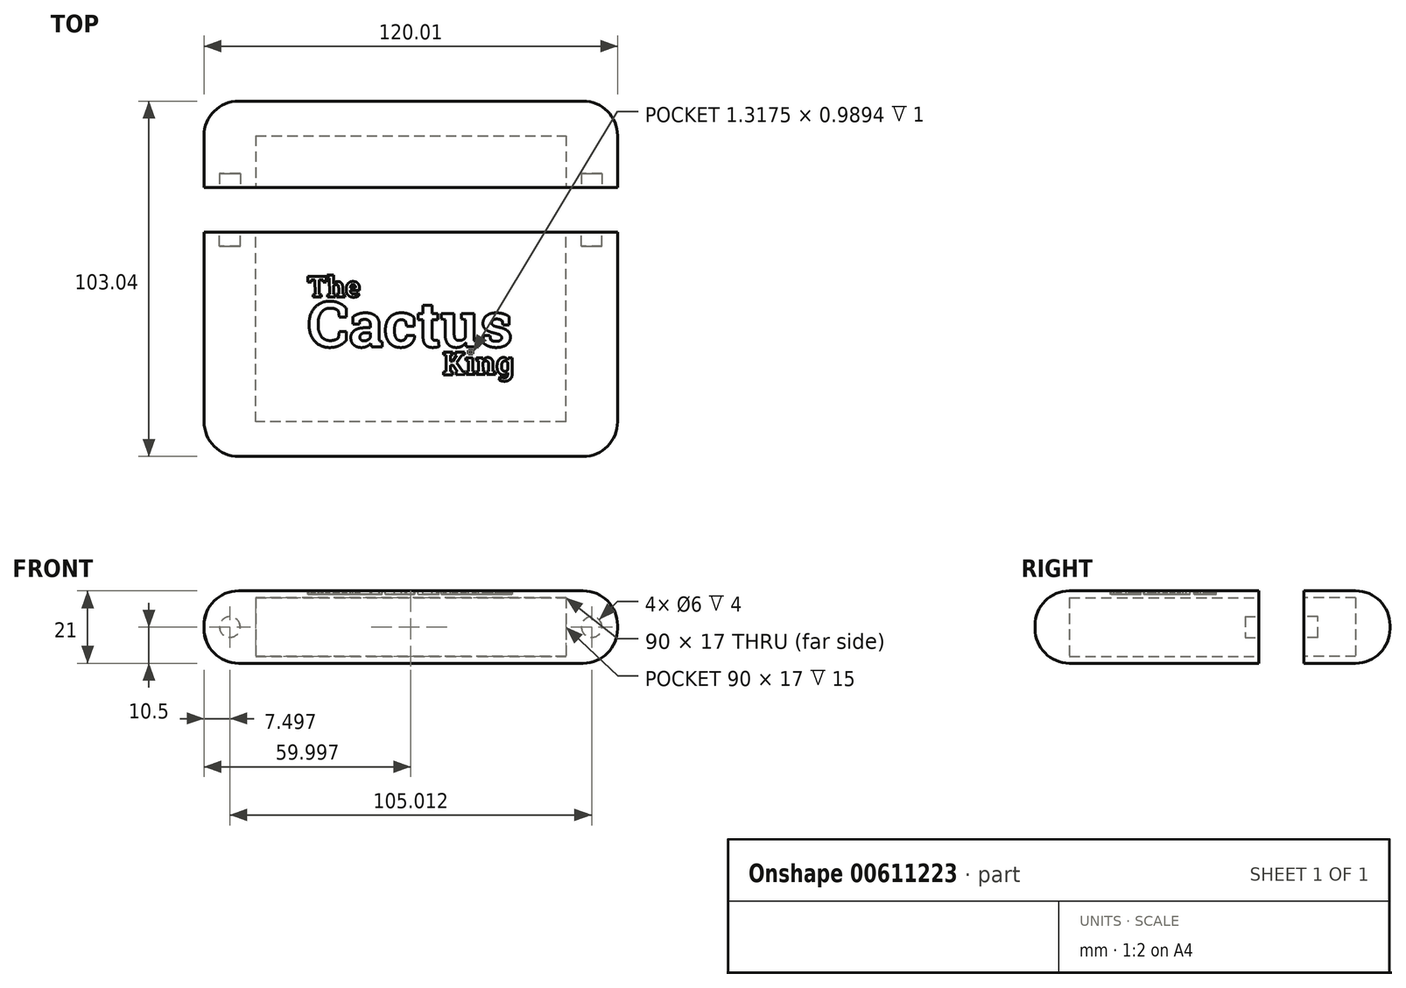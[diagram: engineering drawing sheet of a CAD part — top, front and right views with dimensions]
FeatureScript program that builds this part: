
annotation { "Feature Type Name" : "Feature", "Feature Type Description" : "" }
export const myFeature = defineFeature(function(context is Context, id is Id, definition is map)
    precondition{}
    {
        {
            var Q0;
            Q0=qCreatedBy(makeId("Top.planeOp"),FACE);
            var sketch = newSketch(context, id + "F0", { "sketchPlane" : qUnion([Q0])});
            skLineSegment(sketch, "E0.top", {"start": v(-57.38, -31.8) * mm, "end": v(62.62, -31.8) * mm});
            skLineSegment(sketch, "E0.left", {"start": v(-57.38, 33.2) * mm, "end": v(-57.38, -31.8) * mm});
            skLineSegment(sketch, "E0.right", {"start": v(62.62, 33.2) * mm, "end": v(62.62, -31.8) * mm});
            skLineSegment(sketch, "E1", {"start": v(-57.38, 33.2) * mm, "end": v(62.62, 33.2) * mm});
            skSolve(sketch);
        }
        {
            var Q0;
            Q0=qCreatedBy(makeId("Top.planeOp"),FACE);
            var sketch = newSketch(context, id + "F1", { "sketchPlane" : qUnion([Q0])});
            skLineSegment(sketch, "E2.bottom", {"start": v(-57.4, 71.24) * mm, "end": v(62.6, 71.24) * mm});
            skLineSegment(sketch, "E2.top", {"start": v(-57.4, 46.24) * mm, "end": v(62.6, 46.24) * mm});
            skLineSegment(sketch, "E2.left", {"start": v(-57.4, 71.24) * mm, "end": v(-57.4, 46.24) * mm});
            skLineSegment(sketch, "E2.right", {"start": v(62.6, 71.24) * mm, "end": v(62.6, 46.24) * mm});
            skSolve(sketch);
        }
        {
            var Q0;
            Q0=makeQuery(id+"F1.imprint","IMPRINT",FACE,{"disambiguationData":[TD([[makeQuery(id+"F1.imprint","IMPRINT",EDGE,{"derivedFrom":sQuery(id+"F1.wireOp",EDGE,"E2.bottom")}),-1.0]])]});
            extrude(context, id + "F2", {"entities" : qUnion([Q0]), "depth" : 21 * mm, "offsetDistance" : 25 * mm});
        }
        {
            var Q0;
            Q0=makeQuery(id+"F2.opExtrude","SWEPT_EDGE",EDGE,{"disambiguationData":[OSD([sQuery(id+"F1.wireOp",EDGE,"E2.bottom"),sQuery(id+"F1.wireOp",EDGE,"E2.right")])]});
            var Q1;
            Q1=makeQuery(id+"F2.opExtrude","SWEPT_EDGE",EDGE,{"disambiguationData":[OSD([sQuery(id+"F1.wireOp",EDGE,"E2.bottom"),sQuery(id+"F1.wireOp",EDGE,"E2.left")])]});
            var Q2;
            Q2=makeQuery(id+"F2.opExtrude","CAP_EDGE",EDGE,{"disambiguationData":[OSD([sQuery(id+"F1.wireOp",EDGE,"E2.bottom")])],"isStart":false});
            var Q3;
            Q3=makeQuery(id+"F2.opExtrude","CAP_EDGE",EDGE,{"disambiguationData":[OSD([sQuery(id+"F1.wireOp",EDGE,"E2.bottom")])],"isStart":true});
            var Q4;
            Q4=makeQuery(id+"F2.opExtrude","CAP_EDGE",EDGE,{"disambiguationData":[OSD([sQuery(id+"F1.wireOp",EDGE,"E2.left")])],"isStart":true});
            var Q5;
            Q5=makeQuery(id+"F2.opExtrude","CAP_EDGE",EDGE,{"disambiguationData":[OSD([sQuery(id+"F1.wireOp",EDGE,"E2.left")])],"isStart":false});
            var Q6;
            Q6=makeQuery(id+"F2.opExtrude","CAP_EDGE",EDGE,{"disambiguationData":[OSD([sQuery(id+"F1.wireOp",EDGE,"E2.right")])],"isStart":false});
            var Q7;
            Q7=makeQuery(id+"F2.opExtrude","CAP_EDGE",EDGE,{"disambiguationData":[OSD([sQuery(id+"F1.wireOp",EDGE,"E2.right")])],"isStart":true});
            fillet(context, id + "F3", {"entities" : qUnion([Q0, Q1, Q2, Q3, Q4, Q5, Q6, Q7]), "radius" : 10 * mm, "tangentPropagation" : true, "allowEdgeOverflow" : false});
        }
        {
            var Q0;
            Q0=makeQuery(id+"F2.opExtrude","SWEPT_FACE",FACE,{"disambiguationData":[OSD([sQuery(id+"F1.wireOp",EDGE,"E2.top")])]});
            var sketch = newSketch(context, id + "F4", { "sketchPlane" : qUnion([Q0])});
            skLineSegment(sketch, "E3.bottom", {"start": v(-42.4, 19) * mm, "end": v(47.6, 19) * mm});
            skLineSegment(sketch, "E3.top", {"start": v(-42.4, 2) * mm, "end": v(47.6, 2) * mm});
            skLineSegment(sketch, "E3.left", {"start": v(-42.4, 19) * mm, "end": v(-42.4, 2) * mm});
            skLineSegment(sketch, "E3.right", {"start": v(47.6, 19) * mm, "end": v(47.6, 2) * mm});
            skSolve(sketch);
        }
        {
            var Q0;
            Q0=makeQuery(id+"F4.imprint","IMPRINT",FACE,{"disambiguationData":[TD([[makeQuery(id+"F4.imprint","IMPRINT",EDGE,{"derivedFrom":sQuery(id+"F4.wireOp",EDGE,"E3.bottom")}),-1.0]])]});
            extrude(context, id + "F5", {"entities" : qUnion([Q0]), "operationType" : NewBodyOperationType.REMOVE, "oppositeDirection" : true, "depth" : 15 * mm, "offsetDistance" : 25 * mm});
        }
        {
            var Q0;
            Q0=makeQuery(id+"F2.opExtrude","SWEPT_FACE",FACE,{"disambiguationData":[OSD([sQuery(id+"F1.wireOp",EDGE,"E2.top")])]});
            var sketch = newSketch(context, id + "F6", { "sketchPlane" : qUnion([Q0])});
            skCircle(sketch, "E4", {"center": v(-49.9, 10.5) * mm, "radius": 3 * mm});
            skCircle(sketch, "E5", {"center": v(55.1, 10.5) * mm, "radius": 3 * mm});
            skSolve(sketch);
        }
        {
            var Q0;
            Q0=makeQuery(id+"F6.imprint","IMPRINT",FACE,{"disambiguationData":[TD([[makeQuery(id+"F6.imprint","IMPRINT",EDGE,{"derivedFrom":sQuery(id+"F6.wireOp",EDGE,"E5")}),1.0]])]});
            var Q1;
            Q1=makeQuery(id+"F6.imprint","IMPRINT",FACE,{"disambiguationData":[TD([[makeQuery(id+"F6.imprint","IMPRINT",EDGE,{"derivedFrom":sQuery(id+"F6.wireOp",EDGE,"E4")}),1.0]])]});
            extrude(context, id + "F7", {"entities" : qUnion([Q0, Q1]), "operationType" : NewBodyOperationType.REMOVE, "oppositeDirection" : true, "depth" : 4 * mm, "offsetDistance" : 25 * mm});
        }
        {
            var Q0;
            Q0=makeQuery(id+"F0.imprint","IMPRINT",FACE,{"disambiguationData":[TD([[makeQuery(id+"F0.imprint","IMPRINT",EDGE,{"derivedFrom":sQuery(id+"F0.wireOp",EDGE,"E0.top")}),1.0]])]});
            extrude(context, id + "F8", {"entities" : qUnion([Q0]), "depth" : 21 * mm, "offsetDistance" : 25 * mm});
        }
        {
            var Q0;
            Q0=makeQuery(id+"F8.opExtrude","CAP_EDGE",EDGE,{"disambiguationData":[OSD([sQuery(id+"F0.wireOp",EDGE,"E0.right")])],"isStart":false});
            var Q1;
            Q1=makeQuery(id+"F8.opExtrude","CAP_EDGE",EDGE,{"disambiguationData":[OSD([sQuery(id+"F0.wireOp",EDGE,"E0.right")])],"isStart":true});
            var Q2;
            Q2=makeQuery(id+"F8.opExtrude","CAP_EDGE",EDGE,{"disambiguationData":[OSD([sQuery(id+"F0.wireOp",EDGE,"E0.left")])],"isStart":true});
            var Q3;
            Q3=makeQuery(id+"F8.opExtrude","CAP_EDGE",EDGE,{"disambiguationData":[OSD([sQuery(id+"F0.wireOp",EDGE,"E0.left")])],"isStart":false});
            var Q4;
            Q4=makeQuery(id+"F8.opExtrude","CAP_EDGE",EDGE,{"disambiguationData":[OSD([sQuery(id+"F0.wireOp",EDGE,"E0.top")])],"isStart":false});
            var Q5;
            Q5=makeQuery(id+"F8.opExtrude","CAP_EDGE",EDGE,{"disambiguationData":[OSD([sQuery(id+"F0.wireOp",EDGE,"E0.top")])],"isStart":true});
            var Q6;
            Q6=makeQuery(id+"F8.opExtrude","SWEPT_EDGE",EDGE,{"disambiguationData":[OSD([sQuery(id+"F0.wireOp",EDGE,"E0.top"),sQuery(id+"F0.wireOp",EDGE,"E0.right")])]});
            var Q7;
            Q7=makeQuery(id+"F8.opExtrude","SWEPT_EDGE",EDGE,{"disambiguationData":[OSD([sQuery(id+"F0.wireOp",EDGE,"E0.top"),sQuery(id+"F0.wireOp",EDGE,"E0.left")])]});
            fillet(context, id + "F9", {"entities" : qUnion([Q0, Q1, Q2, Q3, Q4, Q5, Q6, Q7]), "radius" : 10 * mm, "tangentPropagation" : true, "allowEdgeOverflow" : false});
        }
        {
            var Q0;
            Q0=makeQuery(id+"F8.opExtrude","SWEPT_FACE",FACE,{"disambiguationData":[OSD([sQuery(id+"F0.wireOp",EDGE,"E1")])]});
            var sketch = newSketch(context, id + "F10", { "sketchPlane" : qUnion([Q0])});
            skLineSegment(sketch, "E6.bottom", {"start": v(42.38, 19) * mm, "end": v(-47.62, 19) * mm});
            skLineSegment(sketch, "E6.top", {"start": v(42.38, 2) * mm, "end": v(-47.62, 2) * mm});
            skLineSegment(sketch, "E6.left", {"start": v(42.38, 19) * mm, "end": v(42.38, 2) * mm});
            skLineSegment(sketch, "E6.right", {"start": v(-47.62, 19) * mm, "end": v(-47.62, 2) * mm});
            skCircle(sketch, "E7", {"center": v(-55.12, 10.5) * mm, "radius": 3 * mm});
            skCircle(sketch, "E8", {"center": v(49.88, 10.5) * mm, "radius": 3 * mm});
            skSolve(sketch);
        }
        {
            var Q0;
            Q0=makeQuery(id+"F10.imprint","IMPRINT",FACE,{"disambiguationData":[TD([[makeQuery(id+"F10.imprint","IMPRINT",EDGE,{"derivedFrom":sQuery(id+"F10.wireOp",EDGE,"E8")}),1.0]])]});
            var Q1;
            Q1=makeQuery(id+"F10.imprint","IMPRINT",FACE,{"disambiguationData":[TD([[makeQuery(id+"F10.imprint","IMPRINT",EDGE,{"derivedFrom":sQuery(id+"F10.wireOp",EDGE,"E7")}),1.0]])]});
            var Q2;
            Q2=sQuery(id+"F10.wireOp",EDGE,"E8");
            extrude(context, id + "F11", {"entities" : qUnion([Q0, Q1]), "operationType" : NewBodyOperationType.REMOVE, "surfaceEntities" : qUnion([Q2]), "oppositeDirection" : true, "depth" : 4 * mm, "offsetDistance" : 25 * mm});
        }
        {
            var Q0;
            Q0=makeQuery(id+"F8.opExtrude","SWEPT_FACE",FACE,{"disambiguationData":[OSD([sQuery(id+"F0.wireOp",EDGE,"E1")])]});
            var sketch = newSketch(context, id + "F12", { "sketchPlane" : qUnion([Q0])});
            skLineSegment(sketch, "E9.bottom", {"start": v(-47.62, 19) * mm, "end": v(42.38, 19) * mm});
            skLineSegment(sketch, "E9.top", {"start": v(-47.62, 2) * mm, "end": v(42.38, 2) * mm});
            skLineSegment(sketch, "E9.left", {"start": v(-47.62, 19) * mm, "end": v(-47.62, 2) * mm});
            skLineSegment(sketch, "E9.right", {"start": v(42.38, 19) * mm, "end": v(42.38, 2) * mm});
            skSolve(sketch);
        }
        {
            var Q0;
            Q0=makeQuery(id+"F12.imprint","IMPRINT",FACE,{"disambiguationData":[TD([[makeQuery(id+"F12.imprint","IMPRINT",EDGE,{"derivedFrom":sQuery(id+"F12.wireOp",EDGE,"E9.bottom")}),-1.0]])]});
            extrude(context, id + "F13", {"entities" : qUnion([Q0]), "operationType" : NewBodyOperationType.REMOVE, "oppositeDirection" : true, "depth" : 55 * mm, "offsetDistance" : 25 * mm});
        }
        {
            var Q0;
            Q0=makeQuery(id+"F8.opExtrude","CAP_FACE",FACE,{"disambiguationData":[OSD([sQuery(id+"F0.wireOp",EDGE,"E0.top"),sQuery(id+"F0.wireOp",EDGE,"E0.left"),sQuery(id+"F0.wireOp",EDGE,"E0.right"),sQuery(id+"F0.wireOp",EDGE,"E1")])],"isStart":false});
            var sketch = newSketch(context, id + "F14", { "sketchPlane" : qUnion([Q0])});
            skText(sketch, "E10", { "text": "Cactus", "fontName": "RobotoSlab-Bold.ttf"});
            skText(sketch, "E11", { "text": "King", "fontName": "RobotoSlab-Bold.ttf"});
            skText(sketch, "E12", { "text": "The", "fontName": "RobotoSlab-Bold.ttf"});
            const initialGuessF14  = {"E10": [-0.02738, -4e-05, 1, 0, 0.01324], "E11": [0.01188, -0.00812, 1, 0.00395, 0.00663], "E12": [-0.02738, 0.0144, 1, 0.00395, 0.00603]};
            skSetInitialGuess(sketch, initialGuessF14);
            skSolve(sketch);
        }
        {
            var Q0;
            Q0 = qSketchRegion(id + "F14", true);
            extrude(context, id + "F15", {"entities" : qUnion([Q0]), "operationType" : NewBodyOperationType.REMOVE, "oppositeDirection" : true, "depth" : 1 * mm, "offsetDistance" : 25 * mm});
        }
    });
